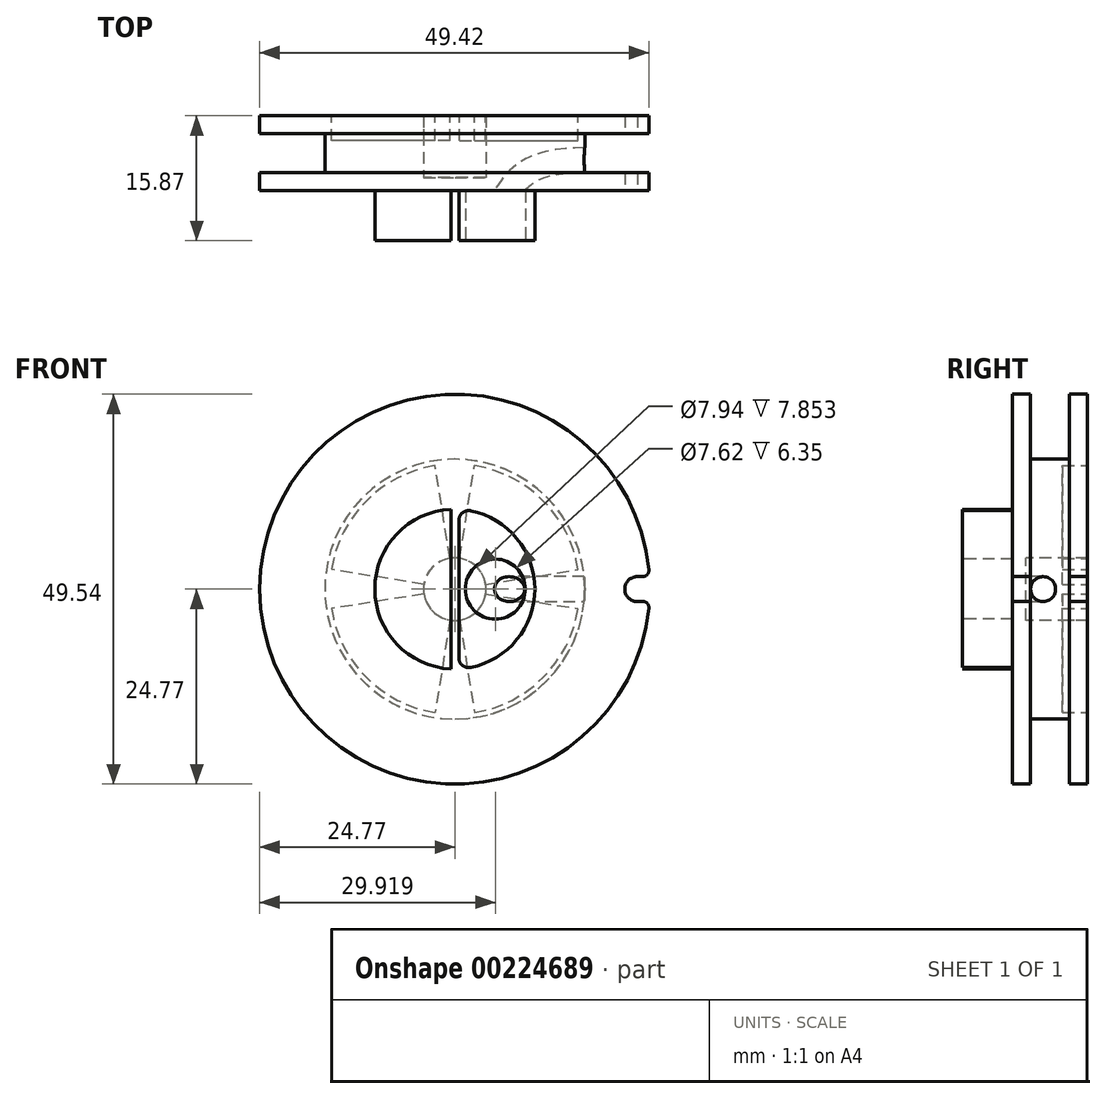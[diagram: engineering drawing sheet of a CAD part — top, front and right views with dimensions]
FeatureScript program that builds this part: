
annotation { "Feature Type Name" : "Feature", "Feature Type Description" : "" }
export const myFeature = defineFeature(function(context is Context, id is Id, definition is map)
    precondition{}
    {
        {
            var Q0;
            Q0=qCreatedBy(makeId("Right.planeOp"),FACE);
            var sketch = newSketch(context, id + "F0", { "sketchPlane" : qUnion([Q0])});
            skLineSegment(sketch, "E0", {"start": v(-9.4, 0) * mm, "end": v(-9.4, 10.16) * mm});
            skLineSegment(sketch, "E1", {"start": v(-9.4, 10.16) * mm, "end": v(-3.05, 10.16) * mm});
            skLineSegment(sketch, "E2", {"start": v(-3.05, 10.16) * mm, "end": v(-3.05, 24.77) * mm});
            skLineSegment(sketch, "E3", {"start": v(-3.05, 24.77) * mm, "end": v(-0.77, 24.77) * mm});
            skLineSegment(sketch, "E4", {"start": v(-0.77, 24.77) * mm, "end": v(-0.77, 16.51) * mm});
            skLineSegment(sketch, "E5", {"start": v(-0.77, 16.51) * mm, "end": v(4.19, 16.51) * mm});
            skLineSegment(sketch, "E6", {"start": v(4.19, 16.51) * mm, "end": v(4.19, 24.77) * mm});
            skLineSegment(sketch, "E7", {"start": v(4.19, 24.77) * mm, "end": v(6.47, 24.77) * mm});
            skLineSegment(sketch, "E8", {"start": v(6.47, 24.77) * mm, "end": v(6.47, 3.97) * mm});
            skLineSegment(sketch, "E9", {"start": v(6.47, 3.97) * mm, "end": v(-1.38, 3.97) * mm});
            skLineSegment(sketch, "E10", {"start": v(-1.38, 3.97) * mm, "end": v(-1.38, 0) * mm});
            skLineSegment(sketch, "E11", {"start": v(-1.38, 0) * mm, "end": v(-9.4, 0) * mm});
            skSolve(sketch);
        }
        {
            var Q0;
            Q0=qCreatedBy(makeId("Right.planeOp"),FACE);
            var sketch = newSketch(context, id + "F1", { "sketchPlane" : qUnion([Q0])});
            skLineSegment(sketch, "E12", {"start": v(0, 0) * mm, "end": v(32.12, 0) * mm});
            skSolve(sketch);
        }
        {
            var Q0;
            Q0 = qSketchRegion(id + "F0", true);
            var Q1;
            Q1=sQuery(id+"F1.wireOp",EDGE,"E12");
            revolve(context, id + "F2", {"entities" : qUnion([Q0]), "axis" : qUnion([Q1]), "revolveType" : RevolveType.FULL});
        }
        {
            var Q0;
            Q0=makeQuery(id+"F2.opRevolve","SWEPT_FACE",FACE,{"disambiguationData":[OSD([sQuery(id+"F0.wireOp",EDGE,"E8")])]});
            var sketch = newSketch(context, id + "F3", { "sketchPlane" : qUnion([Q0])});
            skArc(sketch, "E13", {"start": v(-2.48, 15.68) * mm, "mid": v(-11.23, 11.23) * mm, "end": v(-15.68, 2.48) * mm});
            skArc(sketch, "E14", {"start": v(-0.62, 3.92) * mm, "mid": v(-2.8, 2.8) * mm, "end": v(-3.92, 0.62) * mm});
            skLineSegment(sketch, "E15", {"start": v(-0.62, 3.92) * mm, "end": v(-2.48, 15.68) * mm});
            skLineSegment(sketch, "E16", {"start": v(0.62, 3.92) * mm, "end": v(2.48, 15.68) * mm});
            skLineSegment(sketch, "E17.1.0", {"start": v(-3.92, -0.62) * mm, "end": v(-15.68, -2.48) * mm});
            skLineSegment(sketch, "E17.1.1", {"start": v(-3.92, 0.62) * mm, "end": v(-15.68, 2.48) * mm});
            skLineSegment(sketch, "E17.2.0", {"start": v(0.62, -3.92) * mm, "end": v(2.48, -15.68) * mm});
            skLineSegment(sketch, "E17.2.1", {"start": v(-0.62, -3.92) * mm, "end": v(-2.48, -15.68) * mm});
            skLineSegment(sketch, "E17.3.0", {"start": v(3.92, 0.62) * mm, "end": v(15.68, 2.48) * mm});
            skLineSegment(sketch, "E17.3.1", {"start": v(3.92, -0.62) * mm, "end": v(15.68, -2.48) * mm});
            skArc(sketch, "E18.trimOffspring", {"start": v(15.68, 2.48) * mm, "mid": v(11.23, 11.23) * mm, "end": v(2.48, 15.68) * mm});
            skArc(sketch, "E19.trimOffspring", {"start": v(2.48, -15.68) * mm, "mid": v(11.23, -11.23) * mm, "end": v(15.68, -2.48) * mm});
            skArc(sketch, "E20.trimOffspring", {"start": v(-15.68, -2.48) * mm, "mid": v(-11.23, -11.23) * mm, "end": v(-2.48, -15.68) * mm});
            skArc(sketch, "E21.trimOffspring", {"start": v(3.92, 0.62) * mm, "mid": v(2.8, 2.8) * mm, "end": v(0.62, 3.92) * mm});
            skArc(sketch, "E22.trimOffspring", {"start": v(0.62, -3.92) * mm, "mid": v(2.8, -2.8) * mm, "end": v(3.92, -0.62) * mm});
            skArc(sketch, "E23.trimOffspring", {"start": v(-3.92, -0.62) * mm, "mid": v(-2.8, -2.8) * mm, "end": v(-0.62, -3.92) * mm});
            skSolve(sketch);
        }
        {
            var Q0;
            Q0 = qSketchRegion(id + "F3", true);
            extrude(context, id + "F4", {"entities" : qUnion([Q0]), "operationType" : NewBodyOperationType.REMOVE, "oppositeDirection" : true, "depth" : 3.17 * mm});
        }
        {
            var Q0;
            Q0=makeQuery(id+"F2.opRevolve","SWEPT_FACE",FACE,{"disambiguationData":[OSD([sQuery(id+"F0.wireOp",EDGE,"E0")])]});
            var sketch = newSketch(context, id + "F5", { "sketchPlane" : qUnion([Q0])});
            skLineSegment(sketch, "E24", {"start": v(-0.5, 10.15) * mm, "end": v(-0.5, -10.15) * mm});
            skLineSegment(sketch, "E25", {"start": v(0.5, 10.15) * mm, "end": v(0.5, -10.15) * mm});
            skArc(sketch, "E26", {"start": v(0.5, 10.15) * mm, "mid": v(0, 10.66) * mm, "end": v(-0.5, 10.15) * mm});
            skArc(sketch, "E27", {"start": v(-0.5, -10.15) * mm, "mid": v(0, -10.66) * mm, "end": v(0.5, -10.15) * mm});
            skSolve(sketch);
        }
        {
            var Q0;
            Q0 = qSketchRegion(id + "F5", true);
            var Q1;
            Q1=makeQuery(id+"F2.opRevolve","SWEPT_FACE",FACE,{"disambiguationData":[OSD([sQuery(id+"F0.wireOp",EDGE,"E2")])]});
            extrude(context, id + "F6", {"entities" : qUnion([Q0]), "operationType" : NewBodyOperationType.REMOVE, "endBound" : BoundingType.UP_TO_SURFACE, "oppositeDirection" : true, "endBoundEntityFace" : qUnion([Q1]), "depth" : 25.4 * mm});
        }
        {
            var Q0;
            Q0=makeQuery(id+"F6.boolean.opBoolean","COPY",EDGE,{"derivedFrom":makeQuery(id+"F6.opExtrude","SWEPT_EDGE",EDGE,{"disambiguationData":[OSD([sQuery(id+"F0.wireOp",EDGE,"E0"),sQuery(id+"F0.wireOp",EDGE,"E1"),sQuery(id+"F5.wireOp",EDGE,"E24"),sQuery(id+"F5.wireOp",EDGE,"E27")])]})});
            var Q1;
            Q1=makeQuery(id+"F6.boolean.opBoolean","COPY",EDGE,{"derivedFrom":makeQuery(id+"F6.opExtrude","SWEPT_EDGE",EDGE,{"disambiguationData":[OSD([sQuery(id+"F0.wireOp",EDGE,"E0"),sQuery(id+"F0.wireOp",EDGE,"E1"),sQuery(id+"F5.wireOp",EDGE,"E25"),sQuery(id+"F5.wireOp",EDGE,"E27")])]})});
            var Q2;
            Q2=makeQuery(id+"F6.boolean.opBoolean","COPY",EDGE,{"derivedFrom":makeQuery(id+"F6.opExtrude","SWEPT_EDGE",EDGE,{"disambiguationData":[OSD([sQuery(id+"F0.wireOp",EDGE,"E0"),sQuery(id+"F0.wireOp",EDGE,"E1"),sQuery(id+"F5.wireOp",EDGE,"E25"),sQuery(id+"F5.wireOp",EDGE,"E26")])]})});
            var Q3;
            Q3=makeQuery(id+"F6.boolean.opBoolean","COPY",EDGE,{"derivedFrom":makeQuery(id+"F6.opExtrude","SWEPT_EDGE",EDGE,{"disambiguationData":[OSD([sQuery(id+"F0.wireOp",EDGE,"E0"),sQuery(id+"F0.wireOp",EDGE,"E1"),sQuery(id+"F5.wireOp",EDGE,"E24"),sQuery(id+"F5.wireOp",EDGE,"E26")])]})});
            fillet(context, id + "F7", {"entities" : qUnion([Q0, Q1, Q2, Q3]), "radius" : 1.27 * mm, "tangentPropagation" : true, "allowEdgeOverflow" : false});
        }
        {
            var Q0;
            Q0=qCreatedBy(makeId("Top.planeOp"),FACE);
            var sketch = newSketch(context, id + "F8", { "sketchPlane" : qUnion([Q0])});
            skFitSpline(sketch, "E28", {"points": [v(5.15, -9.4) * mm, v(8.54, -1.2) * mm, v(16.63, 0.82) * mm], "startDerivative": vector(-0.2, 20.93) * mm, "endDerivative": vector(21.02, 0.16) * mm});
            skSolve(sketch);
        }
        {
            var Q0;
            Q0=makeQuery(id+"F6.boolean.opBoolean","SPLIT",FACE,{"disambiguationData":[TD([makeQuery(id+"F6.opExtrude","SWEPT_FACE",FACE,{"disambiguationData":[OSD([sQuery(id+"F5.wireOp",EDGE,"E25")])]})])],"derivedFrom":makeQuery(id+"F2.opRevolve","SWEPT_FACE",FACE,{"disambiguationData":[OSD([sQuery(id+"F0.wireOp",EDGE,"E0")])]})});
            var sketch = newSketch(context, id + "F9", { "sketchPlane" : qUnion([Q0])});
            skCircle(sketch, "E29", {"center": v(5.15, 0) * mm, "radius": 1.59 * mm});
            skSolve(sketch);
        }
        {
            var Q0;
            Q0 = qSketchRegion(id + "F9", true);
            var Q1;
            Q1 = qConstructionFilter(qBodyType(qCreatedBy(id + "F8" ,EDGE), BodyType.WIRE), ConstructionObject.NO);
            sweep(context, id + "F10", {"operationType" : NewBodyOperationType.REMOVE, "profiles" : qUnion([Q0]), "path" : qUnion([Q1])});
        }
        {
            var Q0;
            Q0=makeQuery(id+"F6.boolean.opBoolean","SPLIT",FACE,{"disambiguationData":[TD([makeQuery(id+"F6.opExtrude","SWEPT_FACE",FACE,{"disambiguationData":[OSD([sQuery(id+"F5.wireOp",EDGE,"E25")])]})])],"derivedFrom":makeQuery(id+"F2.opRevolve","SWEPT_FACE",FACE,{"disambiguationData":[OSD([sQuery(id+"F0.wireOp",EDGE,"E0")])]})});
            var sketch = newSketch(context, id + "F11", { "sketchPlane" : qUnion([Q0])});
            skCircle(sketch, "E30", {"center": v(5.15, 0) * mm, "radius": 3.8 * mm});
            skSolve(sketch);
        }
        {
            var Q0;
            Q0 = qSketchRegion(id + "F11", true);
            extrude(context, id + "F12", {"entities" : qUnion([Q0]), "operationType" : NewBodyOperationType.REMOVE, "oppositeDirection" : true, "depth" : 6.35 * mm});
        }
        {
            var Q0;
            {var subQ0=sQuery(id+"F0.wireOp",EDGE,"E2");Q0=makeQuery(id+"F6.boolean.opBoolean","MERGE",FACE,{"derivedFrom":[makeQuery(id+"F2.opRevolve","SWEPT_FACE",FACE,{"disambiguationData":[OSD([subQ0])]}),makeQuery(id+"F6.opExtrude","CAP_FACE",FACE,{"disambiguationData":[OSD([subQ0])],"isStart":false})]});}
            var sketch = newSketch(context, id + "F13", { "sketchPlane" : qUnion([Q0])});
            skArc(sketch, "E31", {"start": v(23.2, 1.59) * mm, "mid": v(21.6, 0) * mm, "end": v(23.22, -1.59) * mm});
            skLineSegment(sketch, "E32", {"start": v(23.2, 1.59) * mm, "end": v(25.55, 1.59) * mm});
            skLineSegment(sketch, "E33", {"start": v(25.55, 1.59) * mm, "end": v(25.55, -1.52) * mm});
            skLineSegment(sketch, "E34", {"start": v(25.55, -1.52) * mm, "end": v(23.22, -1.59) * mm});
            skSolve(sketch);
        }
        {
            var Q0;
            Q0 = qSketchRegion(id + "F13", true);
            extrude(context, id + "F14", {"entities" : qUnion([Q0]), "operationType" : NewBodyOperationType.REMOVE, "endBound" : BoundingType.THROUGH_ALL, "oppositeDirection" : true, "depth" : 25.4 * mm});
        }
        {
            var Q0;
            Q0=makeQuery(id+"F14.boolean.opBoolean","INTERSECT",EDGE,{"derivedFrom":[makeQuery(id+"F2.opRevolve","SWEPT_FACE",FACE,{"disambiguationData":[OSD([sQuery(id+"F0.wireOp",EDGE,"E3")])]}),makeQuery(id+"F14.opExtrude","SWEPT_FACE",FACE,{"disambiguationData":[OSD([sQuery(id+"F13.wireOp",EDGE,"E32")])]})]});
            var Q1;
            Q1=makeQuery(id+"F14.boolean.opBoolean","INTERSECT",EDGE,{"derivedFrom":[makeQuery(id+"F2.opRevolve","SWEPT_FACE",FACE,{"disambiguationData":[OSD([sQuery(id+"F0.wireOp",EDGE,"E3")])]}),makeQuery(id+"F14.opExtrude","SWEPT_FACE",FACE,{"disambiguationData":[OSD([sQuery(id+"F13.wireOp",EDGE,"E34")])]})]});
            var Q2;
            Q2=makeQuery(id+"F14.boolean.opBoolean","INTERSECT",EDGE,{"derivedFrom":[makeQuery(id+"F2.opRevolve","SWEPT_FACE",FACE,{"disambiguationData":[OSD([sQuery(id+"F0.wireOp",EDGE,"E7")])]}),makeQuery(id+"F14.opExtrude","SWEPT_FACE",FACE,{"disambiguationData":[OSD([sQuery(id+"F13.wireOp",EDGE,"E34")])]})]});
            var Q3;
            Q3=makeQuery(id+"F14.boolean.opBoolean","INTERSECT",EDGE,{"derivedFrom":[makeQuery(id+"F2.opRevolve","SWEPT_FACE",FACE,{"disambiguationData":[OSD([sQuery(id+"F0.wireOp",EDGE,"E7")])]}),makeQuery(id+"F14.opExtrude","SWEPT_FACE",FACE,{"disambiguationData":[OSD([sQuery(id+"F13.wireOp",EDGE,"E32")])]})]});
            fillet(context, id + "F15", {"entities" : qUnion([Q0, Q1, Q2, Q3]), "radius" : 0.76 * mm, "tangentPropagation" : true, "allowEdgeOverflow" : false});
        }
    });
